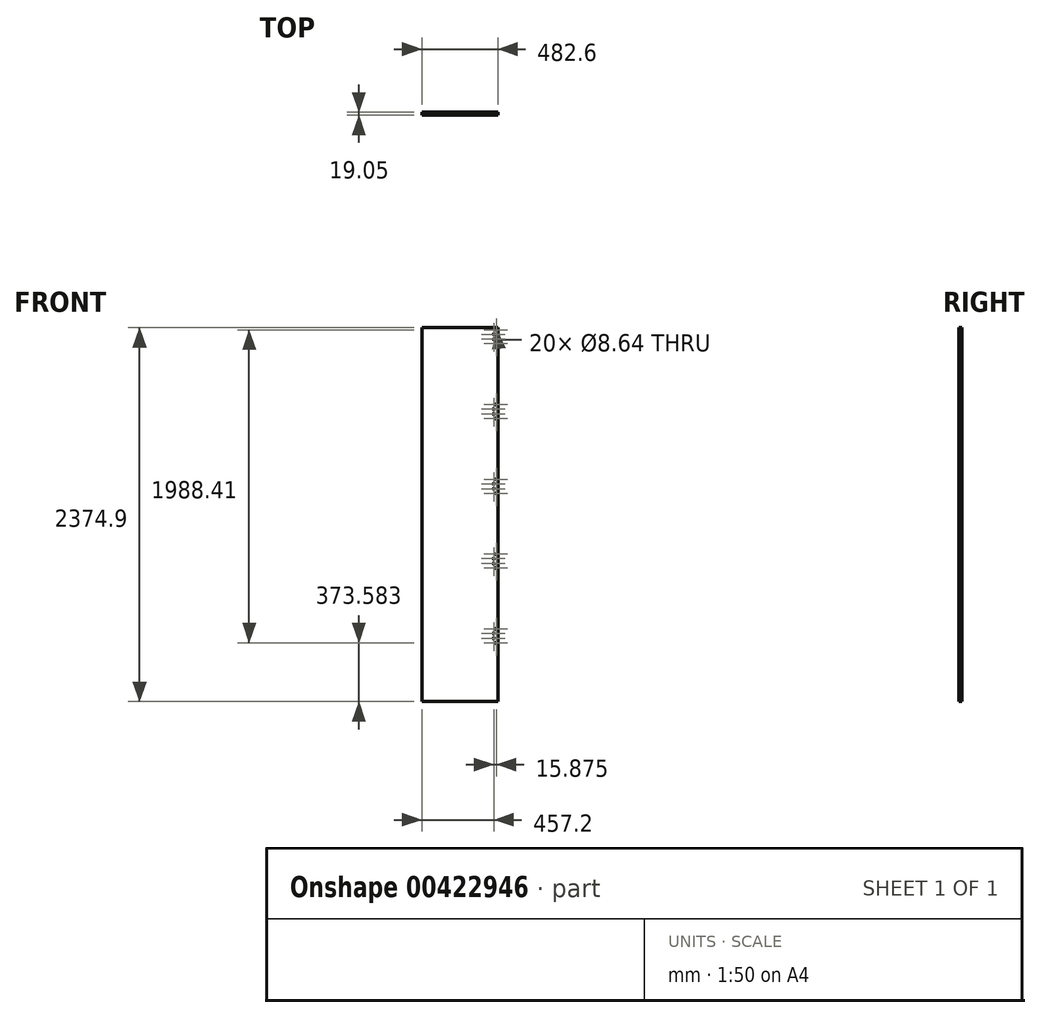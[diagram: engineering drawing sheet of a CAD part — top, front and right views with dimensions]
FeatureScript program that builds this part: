
annotation { "Feature Type Name" : "Feature", "Feature Type Description" : "" }
export const myFeature = defineFeature(function(context is Context, id is Id, definition is map)
    precondition{}
    {
        {
            var Q0;
            Q0=qCreatedBy(makeId("Front.planeOp"),FACE);
            var sketch = newSketch(context, id + "F0", { "sketchPlane" : qUnion([Q0])});
            skLineSegment(sketch, "E0.bottom", {"start": v(241.3, 1187.45) * mm, "end": v(-241.3, 1187.45) * mm});
            skLineSegment(sketch, "E0.top", {"start": v(241.3, -1187.45) * mm, "end": v(-241.3, -1187.45) * mm});
            skLineSegment(sketch, "E0.left", {"start": v(241.3, 1187.45) * mm, "end": v(241.3, -1187.45) * mm});
            skLineSegment(sketch, "E0.right", {"start": v(-241.3, 1187.45) * mm, "end": v(-241.3, -1187.45) * mm});
            skPoint(sketch, "E0.middle", {"position": v(0, 0) * mm});
            skSolve(sketch);
        }
        {
            var Q0;
            Q0 = qSketchRegion(id + "F0", true);
            extrude(context, id + "F1", {"entities" : qUnion([Q0]), "depth" : 19.05 * mm});
        }
        {
            var Q0;
            Q0=makeQuery(id+"F1.opExtrude","CAP_FACE",FACE,{"disambiguationData":[OSD([sQuery(id+"F0.wireOp",EDGE,"E0.bottom"),sQuery(id+"F0.wireOp",EDGE,"E0.top"),sQuery(id+"F0.wireOp",EDGE,"E0.left"),sQuery(id+"F0.wireOp",EDGE,"E0.right")])],"isStart":true});
            var sketch = newSketch(context, id + "F2", { "sketchPlane" : qUnion([Q0])});
            skCircle(sketch, "E1.MirrorC", {"center": v(-215.9, 1145.97) * mm, "radius": 4.32 * mm});
            skCircle(sketch, "E2.MirrorC", {"center": v(-231.78, 1174.55) * mm, "radius": 4.32 * mm});
            skCircle(sketch, "E3.MirrorC", {"center": v(-215.9, 1114.63) * mm, "radius": 4.32 * mm});
            skCircle(sketch, "E4.MirrorC", {"center": v(-231.78, 1086.05) * mm, "radius": 4.32 * mm});
            skCircle(sketch, "E5.MirrorC", {"center": v(-231.78, 699.57) * mm, "radius": 4.32 * mm});
            skCircle(sketch, "E6.MirrorC", {"center": v(-215.9, 671) * mm, "radius": 4.32 * mm});
            skCircle(sketch, "E7.MirrorC", {"center": v(-215.9, 639.65) * mm, "radius": 4.32 * mm});
            skCircle(sketch, "E8.MirrorC", {"center": v(-231.78, 611.07) * mm, "radius": 4.32 * mm});
            skCircle(sketch, "E9.MirrorC", {"center": v(-231.78, 136.1) * mm, "radius": 4.32 * mm});
            skCircle(sketch, "E10.MirrorC", {"center": v(-215.9, 164.67) * mm, "radius": 4.32 * mm});
            skCircle(sketch, "E11.MirrorC", {"center": v(-215.9, 196.01) * mm, "radius": 4.32 * mm});
            skCircle(sketch, "E12.MirrorC", {"center": v(-231.78, 224.59) * mm, "radius": 4.32 * mm});
            skCircle(sketch, "E13.MirrorC", {"center": v(-231.78, -338.89) * mm, "radius": 4.32 * mm});
            skCircle(sketch, "E14.MirrorC", {"center": v(-215.9, -310.31) * mm, "radius": 4.32 * mm});
            skCircle(sketch, "E15.MirrorC", {"center": v(-215.9, -278.97) * mm, "radius": 4.32 * mm});
            skCircle(sketch, "E16.MirrorC", {"center": v(-231.78, -250.4) * mm, "radius": 4.32 * mm});
            skCircle(sketch, "E17.MirrorC", {"center": v(-231.78, -813.87) * mm, "radius": 4.32 * mm});
            skCircle(sketch, "E18.MirrorC", {"center": v(-215.9, -785.3) * mm, "radius": 4.32 * mm});
            skCircle(sketch, "E19.MirrorC", {"center": v(-215.9, -753.95) * mm, "radius": 4.32 * mm});
            skCircle(sketch, "E20.MirrorC", {"center": v(-231.78, -725.37) * mm, "radius": 4.32 * mm});
            skSolve(sketch);
        }
        {
            var Q0;
            Q0 = qSketchRegion(id + "F2", true);
            extrude(context, id + "F3", {"entities" : qUnion([Q0]), "operationType" : NewBodyOperationType.REMOVE, "oppositeDirection" : true, "depth" : 25.4 * mm, "offsetDistance" : 25.4 * mm});
        }
    });
